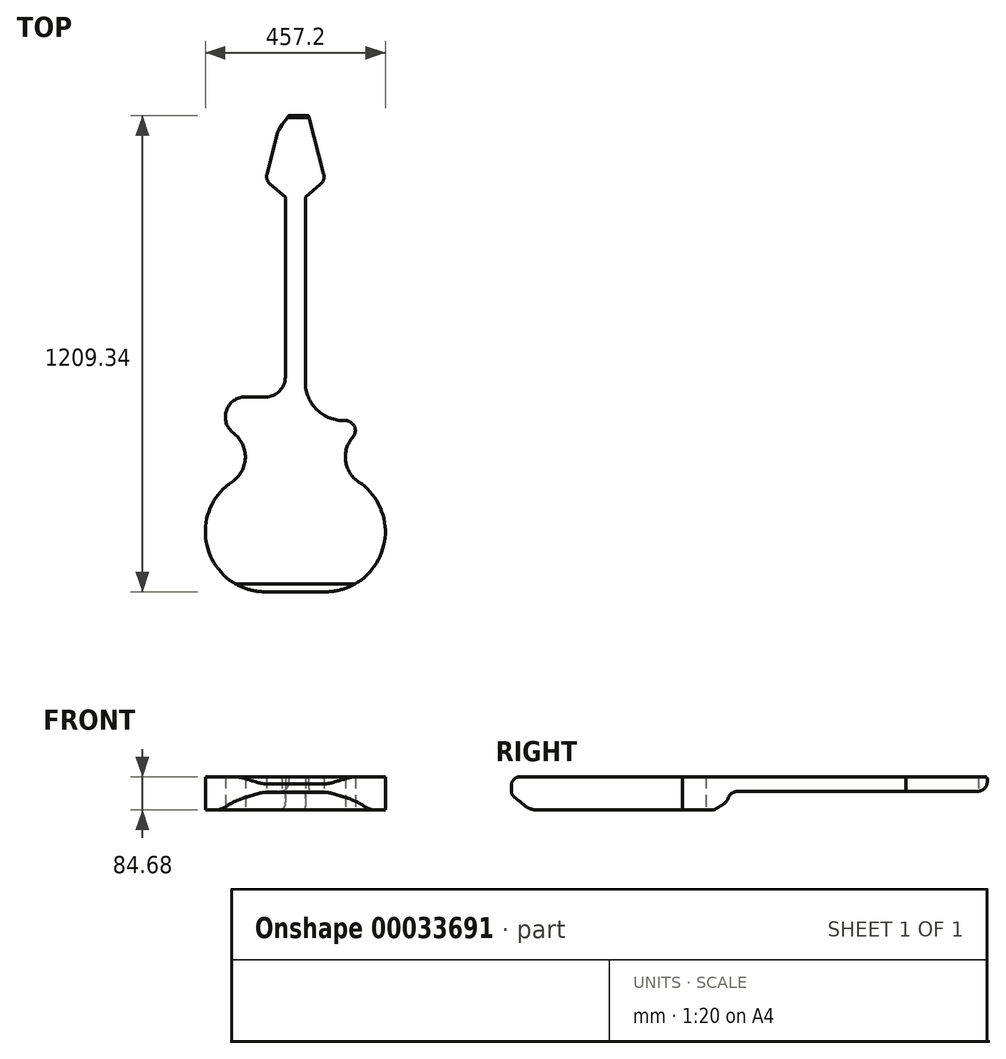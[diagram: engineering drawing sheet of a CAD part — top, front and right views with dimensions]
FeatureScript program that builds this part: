
annotation { "Feature Type Name" : "Feature", "Feature Type Description" : "" }
export const myFeature = defineFeature(function(context is Context, id is Id, definition is map)
    precondition{}
    {
        {
            var Q0;
            Q0=qCreatedBy(makeId("Top.planeOp"),FACE);
            var sketch = newSketch(context, id + "F0", { "sketchPlane" : qUnion([Q0])});
            skArc(sketch, "E0", {"start": v(-84.67, 126.72) * mm, "mid": v(-145.84, -44.24) * mm, "end": v(0, -152.4) * mm});
            skLineSegment(sketch, "E1", {"start": v(0, -152.4) * mm, "end": v(152.4, -152.4) * mm});
            skArc(sketch, "E2", {"start": v(152.4, -152.4) * mm, "mid": v(302.6, -25.77) * mm, "end": v(203.2, 143.68) * mm});
            skArc(sketch, "E3", {"start": v(-84.67, 126.72) * mm, "mid": v(-50.83, 188) * mm, "end": v(-81.28, 251.04) * mm});
            skArc(sketch, "E4", {"start": v(222.25, 240.48) * mm, "mid": v(203.84, 180.23) * mm, "end": v(237.07, 126.72) * mm});
            skLineSegment(sketch, "E5", {"start": v(0, -152.4) * mm, "end": v(-50.8, -152.4) * mm, "construction": true});
            skLineSegment(sketch, "E6", {"start": v(-50.8, -152.4) * mm, "end": v(-50.8, 466.41) * mm, "construction": true});
            skLineSegment(sketch, "E7", {"start": v(152.4, -152.4) * mm, "end": v(203.2, -152.4) * mm, "construction": true});
            skLineSegment(sketch, "E8", {"start": v(203.2, -152.4) * mm, "end": v(203.2, 482.12) * mm, "construction": true});
            skArc(sketch, "E9", {"start": v(-50.8, 342.48) * mm, "mid": v(-99, 307.74) * mm, "end": v(-81.28, 251.04) * mm});
            skLineSegment(sketch, "E10", {"start": v(76.2, -152.4) * mm, "end": v(76.2, 1017.86) * mm, "construction": true});
            skLineSegment(sketch, "E11", {"start": v(-50.8, 342.48) * mm, "end": v(0, 342.48) * mm});
            skLineSegment(sketch, "E12", {"start": v(50.8, 393.28) * mm, "end": v(50.8, 850.48) * mm});
            skLineSegment(sketch, "E13", {"start": v(50.8, 850.48) * mm, "end": v(12.1, 883.5) * mm});
            skLineSegment(sketch, "E14", {"start": v(4, 909.2) * mm, "end": v(31.17, 1013.93) * mm});
            skLineSegment(sketch, "E15", {"start": v(34.4, 1021.28) * mm, "end": v(42.78, 1034.33) * mm});
            skPoint(sketch, "E16.visualSharp", {"position": v(0, 893.82) * mm});
            skArc(sketch, "E16.filletArc", {"start": v(4, 909.2) * mm, "mid": v(4.35, 895.2) * mm, "end": v(12.1, 883.5) * mm});
            skPoint(sketch, "E17.visualSharp", {"position": v(32.2, 1017.86) * mm});
            skArc(sketch, "E17.filletArc", {"start": v(34.4, 1021.28) * mm, "mid": v(32.5, 1017.73) * mm, "end": v(31.17, 1013.93) * mm});
            skPoint(sketch, "E18.visualSharp", {"position": v(52.8, 1049.91) * mm});
            skArc(sketch, "E19.MirrorCS", {"start": v(148.4, 909.2) * mm, "mid": v(148.05, 895.2) * mm, "end": v(140.3, 883.5) * mm});
            skLineSegment(sketch, "E20.MirrorCS", {"start": v(148.4, 909.2) * mm, "end": v(121.23, 1013.93) * mm});
            skLineSegment(sketch, "E21.MirrorCS", {"start": v(101.6, 379.97) * mm, "end": v(101.6, 850.48) * mm});
            skLineSegment(sketch, "E22.MirrorCS", {"start": v(101.6, 850.48) * mm, "end": v(140.3, 883.5) * mm});
            skArc(sketch, "E23", {"start": v(222.25, 240.48) * mm, "mid": v(226.17, 268.13) * mm, "end": v(202.32, 282.66) * mm});
            skArc(sketch, "E24", {"start": v(101.6, 379.97) * mm, "mid": v(131.63, 309.64) * mm, "end": v(203.2, 282.7) * mm});
            skPoint(sketch, "E25.orphan", {"position": v(101.6, 342.48) * mm});
            skPoint(sketch, "E26.visualSharp", {"position": v(50.8, 342.48) * mm});
            skArc(sketch, "E26.filletArc", {"start": v(0, 342.48) * mm, "mid": v(35.92, 357.36) * mm, "end": v(50.8, 393.28) * mm});
            skPoint(sketch, "E27.MirrorCS.end.orphan", {"position": v(109.62, 1034.33) * mm});
            skPoint(sketch, "E27.MirrorCS.start.orphan", {"position": v(118, 1021.28) * mm});
            skPoint(sketch, "E28.MirrorCS.end.orphan", {"position": v(76.2, 1017.86) * mm});
            skPoint(sketch, "E28.MirrorCS.start.orphan", {"position": v(88.68, 1034.95) * mm});
            skPoint(sketch, "E18.filletArc.start.orphan", {"position": v(63.72, 1034.95) * mm});
            skLineSegment(sketch, "E29", {"start": v(42.78, 1034.33) * mm, "end": v(64.78, 1064.82) * mm});
            skLineSegment(sketch, "E30", {"start": v(109.95, 1056.37) * mm, "end": v(148.4, 909.2) * mm});
            skPoint(sketch, "E31.visualSharp", {"position": v(96.33, 1108.53) * mm});
            skArc(sketch, "E31.filletArc", {"start": v(109.95, 1056.37) * mm, "mid": v(90.05, 1074.92) * mm, "end": v(64.78, 1064.82) * mm});
            skSolve(sketch);
        }
        {
            var Q0;
            Q0 = qSketchRegion(id + "F0", true);
            extrude(context, id + "F1", {"entities" : qUnion([Q0]), "depth" : 101.6 * mm});
        }
        {
            var Q0;
            Q0=qCreatedBy(makeId("Right.planeOp"),FACE);
            var sketch = newSketch(context, id + "F2", { "sketchPlane" : qUnion([Q0])});
            skLineSegment(sketch, "E32.top", {"start": v(1031.54, 64.39) * mm, "end": v(422.42, 64.39) * mm});
            skPoint(sketch, "E33.visualSharp", {"position": v(397.02, 64.39) * mm});
            skArc(sketch, "E33.filletArc", {"start": v(422.42, 64.39) * mm, "mid": v(407.41, 59.48) * mm, "end": v(398.2, 46.66) * mm});
            skLineSegment(sketch, "E34", {"start": v(387.8, 33.02) * mm, "end": v(369.24, 21) * mm});
            skLineSegment(sketch, "E35", {"start": v(355.43, 16.92) * mm, "end": v(-86.24, 16.92) * mm});
            skLineSegment(sketch, "E36", {"start": v(-118.59, 28.56) * mm, "end": v(-144.25, 49.75) * mm});
            skLineSegment(sketch, "E37", {"start": v(-153.47, 69.34) * mm, "end": v(-153.47, 76.6) * mm});
            skLineSegment(sketch, "E38", {"start": v(-128.07, 102) * mm, "end": v(1050.6, 102) * mm});
            skLineSegment(sketch, "E39", {"start": v(1056.94, 95.65) * mm, "end": v(1056.94, 89.79) * mm});
            skPoint(sketch, "E40.visualSharp", {"position": v(397.02, 38.99) * mm});
            skArc(sketch, "E40.filletArc", {"start": v(387.8, 33.02) * mm, "mid": v(394.19, 38.94) * mm, "end": v(398.2, 46.66) * mm});
            skPoint(sketch, "E41.visualSharp", {"position": v(362.94, 16.92) * mm});
            skArc(sketch, "E41.filletArc", {"start": v(355.43, 16.92) * mm, "mid": v(362.63, 17.96) * mm, "end": v(369.24, 21) * mm});
            skPoint(sketch, "E42.visualSharp", {"position": v(-104.5, 16.92) * mm});
            skArc(sketch, "E42.filletArc", {"start": v(-118.59, 28.56) * mm, "mid": v(-103.43, 19.92) * mm, "end": v(-86.24, 16.92) * mm});
            skPoint(sketch, "E43.visualSharp", {"position": v(-153.47, 102) * mm});
            skArc(sketch, "E43.filletArc", {"start": v(-128.07, 102) * mm, "mid": v(-137.36, 100.24) * mm, "end": v(-145.36, 95.2) * mm});
            skPoint(sketch, "E44.visualSharp", {"position": v(-153.47, 76.6) * mm});
            skArc(sketch, "E44.filletArc", {"start": v(-145.36, 95.2) * mm, "mid": v(-151.36, 86.75) * mm, "end": v(-153.47, 76.6) * mm});
            skPoint(sketch, "E45.visualSharp", {"position": v(-153.47, 57.37) * mm});
            skArc(sketch, "E45.filletArc", {"start": v(-153.47, 69.34) * mm, "mid": v(-151.05, 58.51) * mm, "end": v(-144.25, 49.75) * mm});
            skPoint(sketch, "E46.visualSharp", {"position": v(1056.94, 102) * mm});
            skArc(sketch, "E46.filletArc", {"start": v(1056.94, 95.65) * mm, "mid": v(1055.08, 100.14) * mm, "end": v(1050.6, 102) * mm});
            skPoint(sketch, "E47.visualSharp", {"position": v(1056.94, 64.39) * mm});
            skArc(sketch, "E47.filletArc", {"start": v(1031.54, 64.39) * mm, "mid": v(1049.5, 71.83) * mm, "end": v(1056.94, 89.79) * mm});
            skLineSegment(sketch, "E48.bottom", {"start": v(-172.35, -72.65) * mm, "end": v(1084.67, -72.65) * mm});
            skLineSegment(sketch, "E48.top", {"start": v(-172.35, 117.01) * mm, "end": v(1084.67, 117.01) * mm});
            skLineSegment(sketch, "E48.left", {"start": v(-172.35, -72.65) * mm, "end": v(-172.35, 117.01) * mm});
            skLineSegment(sketch, "E48.right", {"start": v(1084.67, -72.65) * mm, "end": v(1084.67, 117.01) * mm});
            skSolve(sketch);
        }
        {
            var Q0;
            Q0=makeQuery(id+"F2.imprint","IMPRINT",FACE,{"disambiguationData":[TD([[makeQuery(id+"F2.imprint","IMPRINT",EDGE,{"derivedFrom":sQuery(id+"F2.wireOp",EDGE,"E32.top")}),1.0]])]});
            extrude(context, id + "F3", {"entities" : qUnion([Q0]), "operationType" : NewBodyOperationType.REMOVE, "endBound" : BoundingType.THROUGH_ALL, "depth" : 25.4 * mm});
        }
        {
            var Q0;
            Q0 = qSketchRegion(id + "F2", true);
            extrude(context, id + "F4", {"entities" : qUnion([Q0]), "operationType" : NewBodyOperationType.REMOVE, "endBound" : BoundingType.THROUGH_ALL, "oppositeDirection" : true, "depth" : 25.4 * mm});
        }
    });
